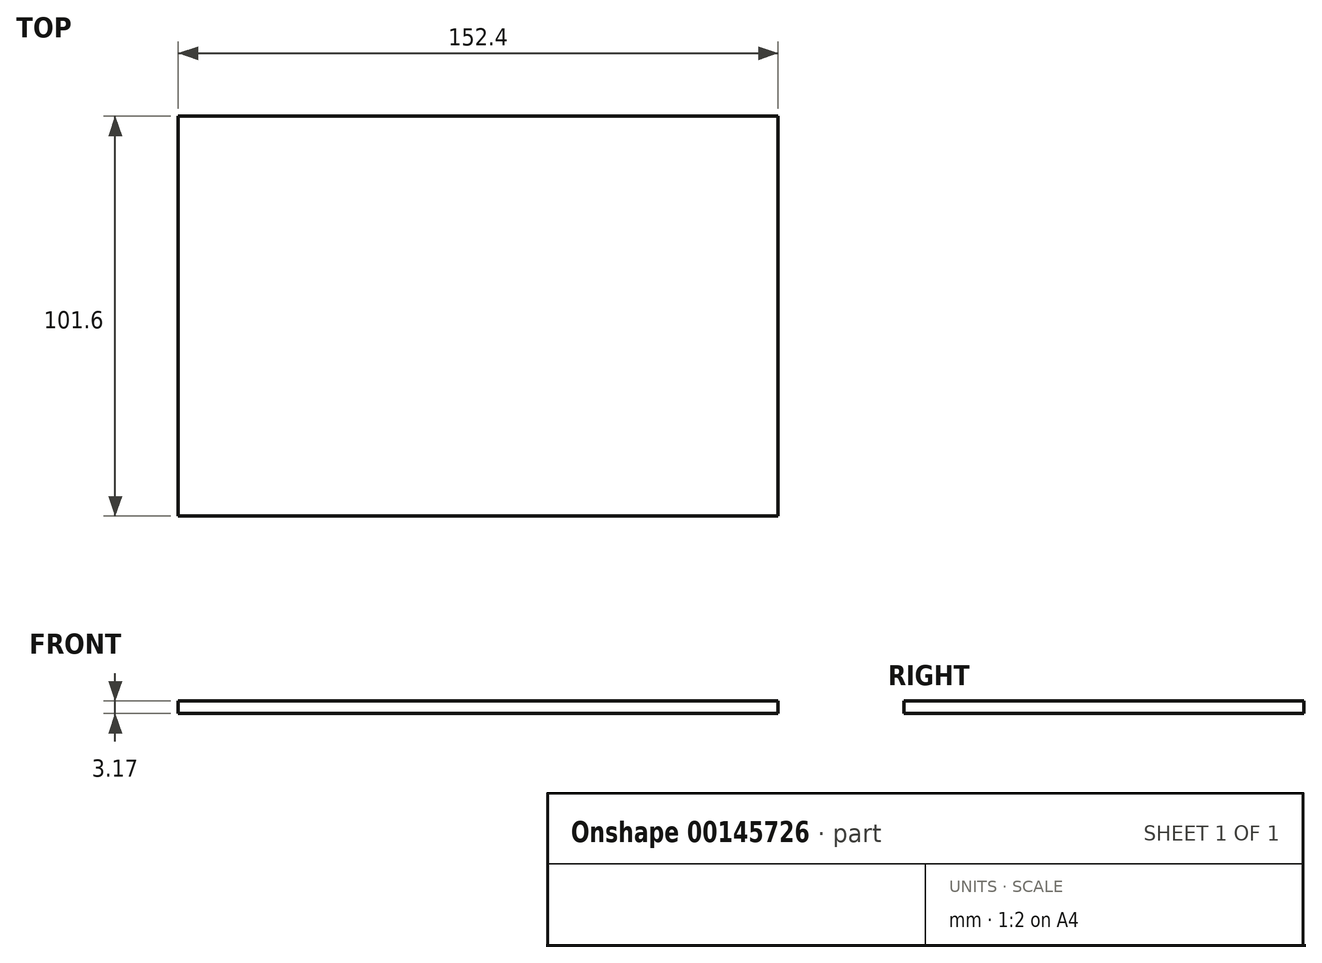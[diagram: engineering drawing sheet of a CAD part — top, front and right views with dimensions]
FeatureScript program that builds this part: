
annotation { "Feature Type Name" : "Feature", "Feature Type Description" : "" }
export const myFeature = defineFeature(function(context is Context, id is Id, definition is map)
    precondition{}
    {
        {
            var Q0;
            Q0=qCreatedBy(makeId("Top.planeOp"),FACE);
            var sketch = newSketch(context, id + "F0", { "sketchPlane" : qUnion([Q0])});
            skLineSegment(sketch, "E0.bottom", {"start": v(76.2, 50.8) * mm, "end": v(-76.2, 50.8) * mm});
            skLineSegment(sketch, "E0.top", {"start": v(76.2, -50.8) * mm, "end": v(-76.2, -50.8) * mm});
            skLineSegment(sketch, "E0.left", {"start": v(76.2, 50.8) * mm, "end": v(76.2, -50.8) * mm});
            skLineSegment(sketch, "E0.right", {"start": v(-76.2, 50.8) * mm, "end": v(-76.2, -50.8) * mm});
            skPoint(sketch, "E0.middle", {"position": v(0, 0) * mm});
            skSolve(sketch);
        }
        {
            var Q0;
            Q0 = qSketchRegion(id + "F0", true);
            extrude(context, id + "F1", {"entities" : qUnion([Q0]), "depth" : 3.17 * mm});
        }
    });
